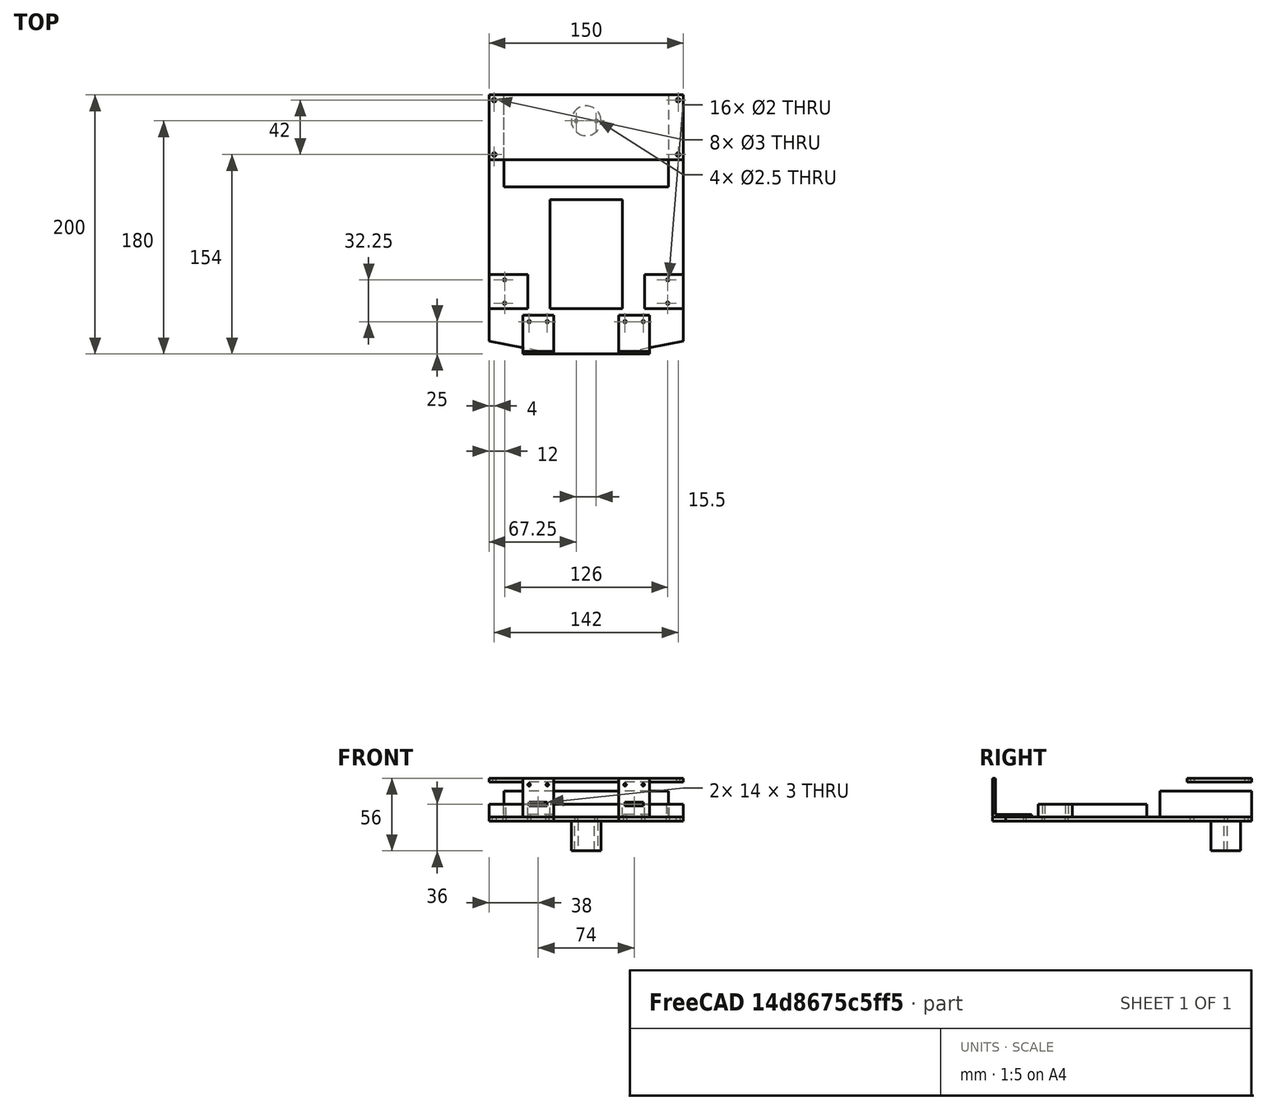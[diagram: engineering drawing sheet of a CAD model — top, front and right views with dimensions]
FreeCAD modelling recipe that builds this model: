
FCSTD DOCUMENT  (FreeCAD 0.20R29177 (Git))
Label: 3mmrobot
License: All rights reserved
LicenseURL: http://en.wikipedia.org/wiki/All_rights_reserved
objects: TechDraw::DrawViewDimension×53, PartDesign::ShapeBinder×16, PartDesign::Pad×11, PartDesign::Pocket×11, PartDesign::Body×10, TechDraw::DrawProjGroupItem×9, Sketcher::SketchObject×7, TechDraw::DrawSVGTemplate×6, TechDraw::DrawProjGroup×6, TechDraw::DrawPage×6, PartDesign::SubShapeBinder×6, TechDraw::DrawViewAnnotation×3, PartDesign::Fillet×2, App::Part×1
note: 87 computed .brp shape members not serialized (recipe doc carries the construction recipe); baked Part::Feature solids carry a one-line shape summary decoded from their .brp

FEATURE [Sketcher::SketchObject] Sketch  label="ChassisOutline"
  FullyConstrained = true
  MapMode = 5
  Support = -> [XY_Plane]
  sketch-geometry (4):
    g0: LineSegment StartX=-75 StartY=100 StartZ=0 EndX=75 EndY=100 EndZ=0
    g1: LineSegment StartX=75 StartY=100 StartZ=0 EndX=75 EndY=-100 EndZ=0
    g2: LineSegment StartX=75 StartY=-100 StartZ=0 EndX=-75 EndY=-100 EndZ=0
    g3: LineSegment StartX=-75 StartY=-100 StartZ=0 EndX=-75 EndY=100 EndZ=0
  constraints (11):
    c: Coincident(g0,g1)
    c: Coincident(g3,g0)
    c: Horizontal(g0)
    c: Vertical(g1)
    c: Vertical(g3)
    c: Distance(g0) = 150
    c: DistanceY(g2,g0) = 200
    c: Coincident(g2,g1)
    c: Coincident(g2,g3)
    c: Symmetric(g1,g0,g-1)
    c: Horizontal(g2)
FEATURE [Sketcher::SketchObject] Sketch001  label="UpperParts"
  AttachmentOffset = pos=(0,0,3) rot=(0,0,1;0rad)
  ExternalGeometry = -> [Sketch]
  FullyConstrained = true
  MapMode = 5
  Placement = pos=(0,0,3) rot=(0,0,1;0rad)
  Support = -> [XY_Plane]
  sketch-geometry (21):
    g0: LineSegment StartX=-63.5 StartY=100 StartZ=0 EndX=63.5 EndY=100 EndZ=0
    g1: LineSegment StartX=63.5 StartY=100 StartZ=0 EndX=63.5 EndY=29 EndZ=0
    g2: LineSegment StartX=63.5 StartY=29 StartZ=0 EndX=-63.5 EndY=29 EndZ=0
    g3: LineSegment StartX=-63.5 StartY=29 StartZ=0 EndX=-63.5 EndY=100 EndZ=0
    g4: LineSegment StartX=-28 StartY=19 StartZ=0 EndX=28 EndY=19 EndZ=0
    g5: LineSegment StartX=28 StartY=19 StartZ=0 EndX=28 EndY=-65 EndZ=0
    g6: LineSegment StartX=28 StartY=-65 StartZ=0 EndX=-28 EndY=-65 EndZ=0
    g7: LineSegment StartX=-28 StartY=-65 StartZ=0 EndX=-28 EndY=19 EndZ=0
    g8: LineSegment StartX=-75 StartY=-65 StartZ=0 EndX=-45 EndY=-65 EndZ=0
    g9: LineSegment StartX=-45 StartY=-65 StartZ=0 EndX=-45 EndY=-38.5 EndZ=0
    g10: LineSegment StartX=-45 StartY=-38.5 StartZ=0 EndX=-75 EndY=-38.5 EndZ=0
    g11: LineSegment StartX=-75 StartY=-38.5 StartZ=0 EndX=-75 EndY=-65 EndZ=0
    g12: LineSegment StartX=75 StartY=-38.5 StartZ=0 EndX=45 EndY=-38.5 EndZ=0
    g13: LineSegment StartX=45 StartY=-38.5 StartZ=0 EndX=45 EndY=-65 EndZ=0
    g14: LineSegment StartX=45 StartY=-65 StartZ=0 EndX=75 EndY=-65 EndZ=0
    g15: LineSegment StartX=75 StartY=-65 StartZ=0 EndX=75 EndY=-38.5 EndZ=0
    g16: Circle CenterX=-63 CenterY=-42.75 CenterZ=0 NormalX=0 NormalY=0 NormalZ=1 AngleXU=0 Radius=1
    g17: Circle CenterX=-63 CenterY=-60.75 CenterZ=0 NormalX=0 NormalY=0 NormalZ=1 AngleXU=0 Radius=1
    g18: Circle CenterX=63 CenterY=-42.75 CenterZ=0 NormalX=0 NormalY=0 NormalZ=1 AngleXU=0 Radius=1
    g19: Circle CenterX=63 CenterY=-60.75 CenterZ=0 NormalX=0 NormalY=0 NormalZ=1 AngleXU=0 Radius=1
    g20: LineSegment StartX=-45 StartY=-51.75 StartZ=0 EndX=-75 EndY=-51.75 EndZ=0
  constraints (57):
    c: Coincident(g0,g1)
    c: Coincident(g1,g2)
    c: Coincident(g2,g3)
    c: Coincident(g3,g0)
    c: Horizontal(g0)
    c: Vertical(g1)
    c: Vertical(g3)
    c: PointOnObject(g0,g-3)
    c: Coincident(g4,g5)
    c: Coincident(g5,g6)
    c: Coincident(g6,g7)
    c: Coincident(g7,g4)
    c: Horizontal(g6)
    c: Vertical(g5)
    c: Vertical(g7)
    c: Distance(g3) = 71
    c: Distance(g2) = 127
    c: Distance(g6) = 56
    c: Distance(g5) = 84
    c: DistanceY(g4,g2) = 10
    c: Symmetric(g2,g1,g-2)
    c: Symmetric(g4,g4,g-2)
    c: Coincident(g8,g9)
    c: Coincident(g9,g10)
    c: Coincident(g10,g11)
    c: Coincident(g11,g8)
    c: Horizontal(g8)
    c: Horizontal(g10)
    c: Vertical(g9)
    c: Vertical(g11)
    c: PointOnObject(g8,g-4)
    c: Coincident(g12,g13)
    c: Coincident(g13,g14)
    c: Coincident(g14,g15)
    c: Coincident(g15,g12)
    c: Horizontal(g12)
    c: Horizontal(g14)
    c: Vertical(g13)
    c: Vertical(g15)
    c: PointOnObject(g12,g-5)
    c: Horizontal(g6,g8)
    c: Equal(g13,g9)
    c: Symmetric(g9,g12,g-2)
    c: DistanceX(g10,g10) = 30
    c: DistanceY(g11,g11) = 26.5
    c: PointOnObject(g20,g9)
    c: PointOnObject(g20,g11)
    c: Symmetric(g10,g8,g20)
    c: Symmetric(g16,g17,g20)
    c: Symmetric(g16,g18,g-2)
    c: Equal(g18,g19)
    c: Equal(g19,g17)
    c: Equal(g17,g16)
    c: Diameter(g16) = 2
    c: DistanceX(g20,g16) = 12
    c: Symmetric(g19,g17,g-2)
    c: DistanceY(g17,g16) = 18
FEATURE [Sketcher::SketchObject] Sketch002  label="LowerParts"
  ExternalGeometry = -> [Sketch]
  FullyConstrained = true
  MapMode = 5
  Support = -> [XY_Plane]
  sketch-geometry (3):
    g0: Circle CenterX=0 CenterY=80 CenterZ=0 NormalX=0 NormalY=0 NormalZ=1 AngleXU=0 Radius=11.5
    g1: Circle CenterX=-7.75 CenterY=80 CenterZ=0 NormalX=0 NormalY=0 NormalZ=1 AngleXU=0 Radius=1.25
    g2: Circle CenterX=7.75 CenterY=80 CenterZ=0 NormalX=0 NormalY=0 NormalZ=1 AngleXU=0 Radius=1.25
  constraints (8):
    c: PointOnObject(g0,g-2)
    c: Symmetric(g1,g2,g-2)
    c: Horizontal(g0,g1)
    c: Diameter(g2) = 2.5
    c: Equal(g2,g1)
    c: Diameter(g0) = 23
    c: DistanceX(g1,g2) = 15.5
    c: DistanceY(g0,g-3) = 20
FEATURE [PartDesign::ShapeBinder] ShapeBinder
  Support = -> [Sketch,Sketch002,Sketch001]
  TraceSupport = false
FEATURE [PartDesign::Pad] Pad
  Direction = (0,0,1)
  Length = 3
  Length2 = 10
  Profile = -> ShapeBinder
  Type = 0
FEATURE [PartDesign::ShapeBinder] ShapeBinder001
  Support = -> [Sketch001]
  TraceSupport = false
FEATURE [PartDesign::Pocket] Pocket
  BaseFeature = -> Pad
  Direction = (0,0,-1)
  Length = 5
  Length2 = 5
  Profile = -> ShapeBinder001
  Type = 1
FEATURE [PartDesign::ShapeBinder] ShapeBinder002
  Support = -> [Sketch001]
  TraceSupport = false
FEATURE [PartDesign::Pad] Pad001
  Direction = (0,0,1)
  Length = 20
  Length2 = 10
  Profile = -> ShapeBinder002
  Type = 0
FEATURE [PartDesign::Body] Body002  label="BatteryBox"
  Group = -> [ShapeBinder002,Pad001]
  Origin = -> Origin002
  Tip = -> Pad001
FEATURE [PartDesign::ShapeBinder] ShapeBinder003
  Support = -> [Sketch001]
  TraceSupport = false
FEATURE [PartDesign::Pad] Pad002
  Direction = (0,0,1)
  Length = 10
  Length2 = 10
  Profile = -> ShapeBinder003
  Type = 0
FEATURE [PartDesign::Body] Body003  label="Breadboard"
  Group = -> [ShapeBinder003,Pad002]
  Origin = -> Origin003
  Tip = -> Pad002
FEATURE [PartDesign::ShapeBinder] ShapeBinder004
  Support = -> [Sketch001]
  TraceSupport = false
FEATURE [PartDesign::Pad] Pad003
  Direction = (0,0,1)
  Length = 10
  Length2 = 10
  Profile = -> ShapeBinder004
  Type = 0
FEATURE [PartDesign::Body] Body004  label="LeftMotor"
  Group = -> [ShapeBinder004,Pad003]
  Origin = -> Origin004
  Tip = -> Pad003
FEATURE [PartDesign::ShapeBinder] ShapeBinder005
  Support = -> [Sketch001]
  TraceSupport = false
FEATURE [PartDesign::Pad] Pad004
  Direction = (0,0,1)
  Length = 10
  Length2 = 10
  Profile = -> ShapeBinder005
  Type = 0
FEATURE [PartDesign::Body] Body005  label="RightMotor"
  Group = -> [ShapeBinder005,Pad004]
  Origin = -> Origin005
  Tip = -> Pad004
FEATURE [PartDesign::ShapeBinder] ShapeBinder006
  Support = -> [Sketch001]
  TraceSupport = false
FEATURE [PartDesign::Pocket] Pocket001
  BaseFeature = -> Pocket
  Direction = (0,0,-1)
  Length = 5
  Length2 = 5
  Profile = -> ShapeBinder006
  Type = 1
FEATURE [PartDesign::ShapeBinder] ShapeBinder007
  Support = -> [Sketch002]
  TraceSupport = false
FEATURE [PartDesign::Pocket] Pocket002
  BaseFeature = -> Pocket001
  Direction = (0,0,-1)
  Length = 5
  Length2 = 5
  Profile = -> ShapeBinder007
  Reversed = true
  Type = 1
FEATURE [PartDesign::ShapeBinder] ShapeBinder008
  Support = -> [Sketch002]
  TraceSupport = false
FEATURE [PartDesign::Pad] Pad005
  Direction = (0,0,1)
  Length = 23
  Length2 = 10
  Profile = -> ShapeBinder008
  Reversed = true
  Type = 0
FEATURE [PartDesign::Body] Body006  label="Castor"
  Group = -> [ShapeBinder008,Pad005]
  Origin = -> Origin006
  Tip = -> Pad005
FEATURE [TechDraw::DrawSVGTemplate] Template
  Height = 297
  Orientation = 0
  Width = 210
FEATURE [Sketcher::SketchObject] Sketch003  label="BevelFront"
  ExternalGeometry = -> [Sketch]
  FullyConstrained = true
  MapMode = 5
  Support = -> [XY_Plane]
  sketch-geometry (6):
    g0: LineSegment StartX=-75 StartY=-90 StartZ=0 EndX=-25 EndY=-100 EndZ=0
    g1: LineSegment StartX=25 StartY=-100 StartZ=0 EndX=75 EndY=-90 EndZ=0
    g2: LineSegment StartX=-75 StartY=-90 StartZ=0 EndX=-75 EndY=-100 EndZ=0
    g3: LineSegment StartX=-25 StartY=-100 StartZ=0 EndX=-75 EndY=-100 EndZ=0
    g4: LineSegment StartX=25 StartY=-100 StartZ=0 EndX=75 EndY=-100 EndZ=0
    g5: LineSegment StartX=75 StartY=-100 StartZ=0 EndX=75 EndY=-90 EndZ=0
  constraints (14):
    c: PointOnObject(g0,g-4)
    c: PointOnObject(g0,g-3)
    c: Symmetric(g1,g0,g-2)
    c: Symmetric(g0,g1,g-2)
    c: DistanceY(g-4,g0) = 10
    c: DistanceX(g0,g1) = 50
    c: Coincident(g2,g0)
    c: Coincident(g2,g-4)
    c: Coincident(g3,g2)
    c: Coincident(g3,g0)
    c: Coincident(g1,g4)
    c: Coincident(g4,g-5)
    c: Coincident(g4,g5)
    c: Coincident(g5,g1)
FEATURE [PartDesign::ShapeBinder] ShapeBinder009
  Support = -> [Sketch003]
  TraceSupport = false
FEATURE [PartDesign::Pocket] Pocket003
  BaseFeature = -> Pocket002
  Direction = (0,0,-1)
  Length = 5
  Length2 = 5
  Profile = -> ShapeBinder009
  Reversed = true
  Type = 1
FEATURE [PartDesign::ShapeBinder] ShapeBinder010
  Support = -> [Sketch003]
  TraceSupport = false
FEATURE [PartDesign::Pocket] Pocket004
  BaseFeature = -> Pocket003
  Direction = (0,0,-1)
  Length = 5
  Length2 = 5
  Profile = -> ShapeBinder010
  Reversed = true
  Type = 1
FEATURE [TechDraw::DrawSVGTemplate] Template001
  Height = 297
  Orientation = 0
  Width = 210
FEATURE [TechDraw::DrawProjGroupItem] ProjItem001  label="Front001"
  CoarseView = false
  Direction = (0,0,1)
  Focus = 100
  HardHidden = false
  IsoCount = 0
  IsoHidden = false
  IsoVisible = false
  LockPosition = true
  Perspective = false
  Rotation = 0
  RotationVector = (-1,0,0)
  ScaleType = 2
  SeamHidden = false
  SeamVisible = true
  SmoothHidden = false
  SmoothVisible = true
  Source = -> [Pocket002]
  Type = 0
  X = 0
  XDirection = (-1,0,0)
  Y = 0
FEATURE [TechDraw::DrawProjGroup] ProjGroup001
  Anchor = -> ProjItem001
  AutoDistribute = true
  LockPosition = false
  ProjectionType = 0
  Rotation = 0
  ScaleType = 0
  Source = -> [Pocket002]
  Views = -> [ProjItem001]
  X = 105
  Y = 148.5
  spacingX = 15
  spacingY = 15
FEATURE [TechDraw::DrawViewDimension] Dimension012
  AngleOverride = false
  Arbitrary = false
  ArbitraryTolerances = false
  EqualTolerance = true
  ExtensionAngle = 0
  FormatSpec = ⌀%.2f
  FormatSpecOverTolerance = %+.2f
  FormatSpecUnderTolerance = %+.2f
  Inverted = false
  LineAngle = 0
  LockPosition = false
  MeasureType = 1
  OverTolerance = 0
  References2D = -> [ProjItem001]
  Rotation = 0
  ScaleType = 0
  TheoreticalExact = false
  Type = 5
  UnderTolerance = 0
  X = 45.3924
  Y = 74.404
FEATURE [TechDraw::DrawViewDimension] Dimension013
  AngleOverride = false
  Arbitrary = false
  ArbitraryTolerances = false
  EqualTolerance = true
  ExtensionAngle = 0
  FormatSpec = ⌀%.2f
  FormatSpecOverTolerance = %+.2f
  FormatSpecUnderTolerance = %+.2f
  Inverted = false
  LineAngle = 0
  LockPosition = false
  MeasureType = 1
  OverTolerance = 0
  References2D = -> [ProjItem001]
  Rotation = 0
  ScaleType = 0
  TheoreticalExact = false
  Type = 5
  UnderTolerance = 0
  X = 22.3571
  Y = -61.4242
FEATURE [TechDraw::DrawPage] Page001  label="ChassisWithoutBevelsAllDimensions"
  KeepUpdated = true
  NextBalloonIndex = 1
  ProjectionType = 0
  Template = -> Template001
  Views = -> [ProjGroup001,Dimension012,Dimension013]
FEATURE [TechDraw::DrawSVGTemplate] Template002
  Height = 297
  Orientation = 0
  Width = 210
FEATURE [Sketcher::SketchObject] Sketch004  label="DaughterCardOutline"
  AttachmentOffset = pos=(0,0,30) rot=(0,0,1;0rad)
  ExternalGeometry = -> [Sketch]
  FullyConstrained = true
  MapMode = 5
  Placement = pos=(0,0,30) rot=(0,0,1;0rad)
  Support = -> [XY_Plane]
  sketch-geometry (8):
    g0: LineSegment StartX=-75 StartY=100 StartZ=0 EndX=75 EndY=100 EndZ=0
    g1: LineSegment StartX=75 StartY=100 StartZ=0 EndX=75 EndY=50 EndZ=0
    g2: LineSegment StartX=75 StartY=50 StartZ=0 EndX=-75 EndY=50 EndZ=0
    g3: LineSegment StartX=-75 StartY=50 StartZ=0 EndX=-75 EndY=100 EndZ=0
    g4: Circle CenterX=-71 CenterY=96 CenterZ=0 NormalX=0 NormalY=0 NormalZ=1 AngleXU=0 Radius=1.5
    g5: Circle CenterX=-71 CenterY=54 CenterZ=0 NormalX=0 NormalY=0 NormalZ=1 AngleXU=0 Radius=1.5
    g6: Circle CenterX=71 CenterY=96 CenterZ=0 NormalX=0 NormalY=0 NormalZ=1 AngleXU=0 Radius=1.5
    g7: Circle CenterX=71 CenterY=54 CenterZ=0 NormalX=0 NormalY=0 NormalZ=1 AngleXU=0 Radius=1.5
  constraints (22):
    c: Coincident(g0,g1)
    c: Coincident(g1,g2)
    c: Coincident(g2,g3)
    c: Coincident(g3,g0)
    c: Horizontal(g0)
    c: Horizontal(g2)
    c: Vertical(g1)
    c: Vertical(g3)
    c: Coincident(g0,g-4)
    c: PointOnObject(g1,g-5)
    c: DistanceY(g3,g3) = 50
    c: DistanceY(g4,g0) = 4
    c: DistanceX(g0,g4) = 4
    c: Vertical(g5,g4)
    c: Horizontal(g5,g7)
    c: Equal(g6,g4)
    c: Equal(g4,g5)
    c: Equal(g5,g7)
    c: Diameter(g6) = 3
    c: Vertical(g6,g7)
    c: Symmetric(g4,g6,g-2)
    c: DistanceY(g2,g5) = 4
FEATURE [PartDesign::ShapeBinder] ShapeBinder011
  Support = -> [Sketch004]
  TraceSupport = false
FEATURE [PartDesign::Pocket] Pocket005
  BaseFeature = -> Pocket004
  Direction = (0,0,-1)
  Length = 5
  Length2 = 5
  Profile = -> ShapeBinder011
  Reversed = true
  Type = 1
FEATURE [PartDesign::ShapeBinder] ShapeBinder012
  Support = -> [Sketch004]
  TraceSupport = false
FEATURE [PartDesign::Pad] Pad006
  Direction = (0,0,1)
  Length = 3
  Length2 = 10
  Profile = -> ShapeBinder012
  Type = 0
FEATURE [PartDesign::Body] Body007  label="DaughterCard"
  Group = -> [ShapeBinder012,Pad006]
  Origin = -> Origin007
  Tip = -> Pad006
FEATURE [TechDraw::DrawSVGTemplate] Template003
  Height = 297
  Orientation = 0
  Width = 210
FEATURE [TechDraw::DrawProjGroupItem] ProjItem003  label="Front003"
  CoarseView = false
  Direction = (0,0,1)
  Focus = 100
  HardHidden = false
  IsoCount = 0
  IsoHidden = false
  IsoVisible = false
  LockPosition = true
  Perspective = false
  Rotation = 0
  RotationVector = (1,0,0)
  ScaleType = 2
  SeamHidden = false
  SeamVisible = true
  SmoothHidden = false
  SmoothVisible = true
  Source = -> [Body007]
  Type = 0
  X = 0
  XDirection = (1,0,0)
  Y = 0
FEATURE [TechDraw::DrawProjGroup] ProjGroup003
  Anchor = -> ProjItem003
  AutoDistribute = true
  LockPosition = false
  ProjectionType = 0
  Rotation = 0
  ScaleType = 0
  Source = -> [Body007]
  Views = -> [ProjItem003]
  X = 104.394
  Y = 152.44
  spacingX = 15
  spacingY = 15
FEATURE [TechDraw::DrawViewDimension] Dimension028
  AngleOverride = false
  Arbitrary = false
  ArbitraryTolerances = false
  EqualTolerance = true
  ExtensionAngle = 0
  FormatSpec = %.2f
  FormatSpecOverTolerance = %+.2f
  FormatSpecUnderTolerance = %+.2f
  Inverted = false
  LineAngle = 0
  LockPosition = false
  MeasureType = 1
  OverTolerance = 0
  References2D = -> [ProjItem003]
  Rotation = 0
  ScaleType = 0
  TheoreticalExact = false
  Type = 1
  UnderTolerance = 0
  X = 0
  Y = 39.9255
FEATURE [TechDraw::DrawViewDimension] Dimension029
  AngleOverride = false
  Arbitrary = false
  ArbitraryTolerances = false
  EqualTolerance = true
  ExtensionAngle = 0
  FormatSpec = %.2f
  FormatSpecOverTolerance = %+.2f
  FormatSpecUnderTolerance = %+.2f
  Inverted = false
  LineAngle = 0
  LockPosition = false
  MeasureType = 1
  OverTolerance = 0
  References2D = -> [ProjItem003]
  Rotation = 0
  ScaleType = 0
  TheoreticalExact = false
  Type = 1
  UnderTolerance = 0
  X = -62.1643
  Y = 16.3949
FEATURE [TechDraw::DrawViewDimension] Dimension030
  AngleOverride = false
  Arbitrary = false
  ArbitraryTolerances = false
  EqualTolerance = true
  ExtensionAngle = 0
  FormatSpec = %.2f
  FormatSpecOverTolerance = %+.2f
  FormatSpecUnderTolerance = %+.2f
  Inverted = false
  LineAngle = 0
  LockPosition = false
  MeasureType = 1
  OverTolerance = 0
  References2D = -> [ProjItem003]
  Rotation = 0
  ScaleType = 0
  TheoreticalExact = false
  Type = 2
  UnderTolerance = 0
  X = -50.209
  Y = 15.356
FEATURE [TechDraw::DrawViewDimension] Dimension031
  AngleOverride = false
  Arbitrary = false
  ArbitraryTolerances = false
  EqualTolerance = true
  ExtensionAngle = 0
  FormatSpec = %.2f
  FormatSpecOverTolerance = %+.2f
  FormatSpecUnderTolerance = %+.2f
  Inverted = false
  LineAngle = 0
  LockPosition = false
  MeasureType = 1
  OverTolerance = 0
  References2D = -> [ProjItem003]
  Rotation = 0
  ScaleType = 0
  TheoreticalExact = false
  Type = 2
  UnderTolerance = 0
  X = -83.5302
  Y = 3.19164
FEATURE [TechDraw::DrawViewDimension] Dimension032
  AngleOverride = false
  Arbitrary = false
  ArbitraryTolerances = false
  EqualTolerance = true
  ExtensionAngle = 0
  FormatSpec = ⌀%.2f
  FormatSpecOverTolerance = %+.2f
  FormatSpecUnderTolerance = %+.2f
  Inverted = false
  LineAngle = 0
  LockPosition = false
  MeasureType = 1
  OverTolerance = 0
  References2D = -> [ProjItem003]
  Rotation = 0
  ScaleType = 0
  TheoreticalExact = false
  Type = 5
  UnderTolerance = 0
  X = -57.1755
  Y = -10.3746
FEATURE [TechDraw::DrawPage] Page003  label="DaughterCardDimensions"
  KeepUpdated = true
  NextBalloonIndex = 1
  ProjectionType = 0
  Template = -> Template003
  Views = -> [ProjGroup003,Dimension028,Dimension029,Dimension030,Dimension031,Dimension032]
FEATURE [App::Part] Part
  Origin = -> Origin008
FEATURE [Sketcher::SketchObject] Sketch005  label="SensorBracketBase"
  AttachmentOffset = pos=(0,0,3) rot=(0,0,1;0rad)
  ExternalGeometry = -> [Sketch]
  FullyConstrained = true
  MapMode = 5
  Placement = pos=(0,0,3) rot=(0,0,1;0rad)
  Support = -> [XY_Plane]
  sketch-geometry (13):
    g0: LineSegment StartX=-49 StartY=-100 StartZ=0 EndX=-25 EndY=-100 EndZ=0
    g1: LineSegment StartX=-25 StartY=-100 StartZ=0 EndX=-25 EndY=-70 EndZ=0
    g2: LineSegment StartX=-25 StartY=-70 StartZ=0 EndX=-49 EndY=-70 EndZ=0
    g3: LineSegment StartX=-49 StartY=-70 StartZ=0 EndX=-49 EndY=-100 EndZ=0
    g4: LineSegment StartX=25 StartY=-100 StartZ=0 EndX=49 EndY=-100 EndZ=0
    g5: LineSegment StartX=49 StartY=-100 StartZ=0 EndX=49 EndY=-70 EndZ=0
    g6: LineSegment StartX=49 StartY=-70 StartZ=0 EndX=25 EndY=-70 EndZ=0
    g7: LineSegment StartX=25 StartY=-70 StartZ=0 EndX=25 EndY=-100 EndZ=0
    g8: Circle CenterX=-30 CenterY=-75 CenterZ=0 NormalX=0 NormalY=0 NormalZ=1 AngleXU=0 Radius=1
    g9: Circle CenterX=-44 CenterY=-75 CenterZ=0 NormalX=0 NormalY=0 NormalZ=1 AngleXU=0 Radius=1
    g10: Circle CenterX=30 CenterY=-75 CenterZ=0 NormalX=0 NormalY=0 NormalZ=1 AngleXU=0 Radius=1
    g11: Circle CenterX=44 CenterY=-75 CenterZ=0 NormalX=0 NormalY=0 NormalZ=1 AngleXU=0 Radius=1
    g12: LineSegment StartX=-37 StartY=-70 StartZ=0 EndX=-37 EndY=-100 EndZ=0
  constraints (35):
    c: Coincident(g0,g1)
    c: Coincident(g1,g2)
    c: Coincident(g2,g3)
    c: Coincident(g3,g0)
    c: Horizontal(g0)
    c: Horizontal(g2)
    c: Vertical(g1)
    c: Vertical(g3)
    c: PointOnObject(g0,g-3)
    c: Coincident(g4,g5)
    c: Coincident(g5,g6)
    c: Coincident(g6,g7)
    c: Coincident(g7,g4)
    c: Horizontal(g4)
    c: Horizontal(g6)
    c: Vertical(g5)
    c: Vertical(g7)
    c: PointOnObject(g4,g-3)
    c: DistanceY(g1,g1) = 30
    c: Equal(g2,g6)
    c: Symmetric(g1,g6,g-2)
    c: DistanceX(g2,g2) = 24
    c: DistanceX(g0,g4) = 50
    c: PointOnObject(g12,g2)
    c: PointOnObject(g12,g0)
    c: Symmetric(g2,g1,g12)
    c: Symmetric(g9,g8,g12)
    c: Symmetric(g8,g10,g-2)
    c: Symmetric(g11,g9,g-2)
    c: Equal(g9,g8)
    c: Equal(g8,g10)
    c: Equal(g10,g11)
    c: Diameter(g9) = 2
    c: DistanceX(g9,g8) = 14
    c: DistanceY(g9,g2) = 5
FEATURE [PartDesign::ShapeBinder] ShapeBinder013
  Support = -> [Sketch005]
  TraceSupport = false
FEATURE [PartDesign::Pad] Pad007
  Direction = (0,0,1)
  Length = 2
  Length2 = 10
  Profile = -> ShapeBinder013
  Type = 0
FEATURE [PartDesign::ShapeBinder] ShapeBinder014
  Support = -> [Sketch005]
  TraceSupport = false
FEATURE [PartDesign::Pad] Pad008
  Direction = (0,0,1)
  Length = 2
  Length2 = 10
  Profile = -> ShapeBinder014
  Type = 0
FEATURE [Sketcher::SketchObject] Sketch007  label="SensorBracketFront"
  AttachmentOffset = pos=(0,0,100) rot=(0,0,1;0rad)
  ExternalGeometry = -> [Sketch005]
  FullyConstrained = true
  MapMode = 5
  Placement = pos=(0,-100,-2.22e-14) rot=(1,0,0;1.5708rad)
  Support = -> [XZ_Plane]
  sketch-geometry (21):
    g0: LineSegment StartX=-49 StartY=3 StartZ=0 EndX=-25 EndY=3 EndZ=0
    g1: LineSegment StartX=-25 StartY=3 StartZ=0 EndX=-25 EndY=33 EndZ=0
    g2: LineSegment StartX=-25 StartY=33 StartZ=0 EndX=-49 EndY=33 EndZ=0
    g3: LineSegment StartX=-49 StartY=33 StartZ=0 EndX=-49 EndY=3 EndZ=0
    g4: LineSegment StartX=-37 StartY=33 StartZ=0 EndX=-37 EndY=3 EndZ=0
    g5: Circle CenterX=-44 CenterY=28 CenterZ=0 NormalX=0 NormalY=0 NormalZ=1 AngleXU=0 Radius=1
    g6: Circle CenterX=-30 CenterY=28 CenterZ=0 NormalX=0 NormalY=0 NormalZ=1 AngleXU=0 Radius=1
    g7: LineSegment StartX=25 StartY=3 StartZ=0 EndX=49 EndY=3 EndZ=0
    g8: LineSegment StartX=49 StartY=3 StartZ=0 EndX=49 EndY=33 EndZ=0
    g9: LineSegment StartX=49 StartY=33 StartZ=0 EndX=25 EndY=33 EndZ=0
    g10: LineSegment StartX=25 StartY=33 StartZ=0 EndX=25 EndY=3 EndZ=0
    g11: Circle CenterX=30 CenterY=28 CenterZ=0 NormalX=0 NormalY=0 NormalZ=1 AngleXU=0 Radius=1
    g12: Circle CenterX=44 CenterY=28 CenterZ=0 NormalX=0 NormalY=0 NormalZ=1 AngleXU=0 Radius=1
    g13: LineSegment StartX=-44 StartY=11.5 StartZ=0 EndX=-30 EndY=11.5 EndZ=0
    g14: LineSegment StartX=-30 StartY=11.5 StartZ=0 EndX=-30 EndY=14.5 EndZ=0
    g15: LineSegment StartX=-30 StartY=14.5 StartZ=0 EndX=-44 EndY=14.5 EndZ=0
    g16: LineSegment StartX=-44 StartY=14.5 StartZ=0 EndX=-44 EndY=11.5 EndZ=0
    g17: LineSegment StartX=30 StartY=14.5 StartZ=0 EndX=44 EndY=14.5 EndZ=0
    g18: LineSegment StartX=44 StartY=14.5 StartZ=0 EndX=44 EndY=11.5 EndZ=0
    g19: LineSegment StartX=44 StartY=11.5 StartZ=0 EndX=30 EndY=11.5 EndZ=0
    g20: LineSegment StartX=30 StartY=11.5 StartZ=0 EndX=30 EndY=14.5 EndZ=0
  constraints (53):
    c: Coincident(g0,g1)
    c: Coincident(g1,g2)
    c: Coincident(g2,g3)
    c: Coincident(g3,g0)
    c: Horizontal(g2)
    c: Vertical(g1)
    c: Vertical(g3)
    c: Coincident(g0,g-3)
    c: Coincident(g0,g-3)
    c: DistanceY(g3,g3) = 30
    c: PointOnObject(g4,g2)
    c: PointOnObject(g4,g0)
    c: Symmetric(g1,g2,g4)
    c: Coincident(g7,g8)
    c: Coincident(g8,g9)
    c: Coincident(g9,g10)
    c: Coincident(g10,g7)
    c: Horizontal(g9)
    c: Vertical(g8)
    c: Vertical(g10)
    c: Coincident(g7,g-4)
    c: Coincident(g7,g-4)
    c: Equal(g1,g10)
    c: Symmetric(g12,g5,g-2)
    c: Symmetric(g6,g11,g-2)
    c: Equal(g5,g6)
    c: Equal(g6,g11)
    c: Equal(g11,g12)
    c: Symmetric(g6,g5,g4)
    c: Diameter(g5) = 2
    c: DistanceX(g5,g6) = 14
    c: DistanceY(g5,g2) = 5
    c: Coincident(g13,g14)
    c: Coincident(g14,g15)
    c: Coincident(g15,g16)
    c: Coincident(g16,g13)
    c: Horizontal(g15)
    c: Vertical(g14)
    c: Vertical(g16)
    c: Symmetric(g13,g13,g4)
    c: DistanceX(g13,g13) = 14
    c: DistanceY(g13,g6) = 16.5
    c: DistanceY(g14,g14) = 3
    c: Coincident(g17,g18)
    c: Coincident(g18,g19)
    c: Coincident(g19,g20)
    c: Coincident(g20,g17)
    c: Horizontal(g17)
    c: Horizontal(g19)
    c: Vertical(g18)
    c: Vertical(g20)
    c: Symmetric(g17,g14,g-2)
    c: Symmetric(g13,g18,g-2)
FEATURE [PartDesign::Body] Body  label="SketchMain"
  Group = -> [Sketch,Sketch001,Sketch002,Sketch003,Sketch004,Sketch005,Sketch007]
  Origin = -> Origin
FEATURE [PartDesign::ShapeBinder] ShapeBinder015
  Support = -> [Sketch007]
  TraceSupport = false
FEATURE [PartDesign::Pad] Pad009
  BaseFeature = -> Pad007
  Direction = (0,1,4e-16)
  Length = 2
  Length2 = 10
  Profile = -> ShapeBinder015
  Type = 0
FEATURE [PartDesign::SubShapeBinder] Binder
  BindCopyOnChange = 0
  BindMode = 0
  ClaimChildren = false
  Context = -> Body009 [Binder.]
  Fuse = false
  MakeFace = true
  OffsetFill = false
  OffsetIntersection = false
  OffsetJoinType = 0
  OffsetOpenResult = false
  PartialLoad = false
  Relative = true
  Support = -> [Body[Sketch007.Edge11,Sketch007.Edge12,Sketch007.Edge9,Sketch007.Edge10,Sketch007.Edge8,Sketch007.Edge7]]
  _Version = 2
FEATURE [PartDesign::Pad] Pad010
  BaseFeature = -> Pad008
  Direction = (0,1,4e-16)
  Length = 2
  Length2 = 10
  Profile = -> Binder
  Type = 0
FEATURE [PartDesign::SubShapeBinder] Binder001
  BindCopyOnChange = 0
  BindMode = 0
  ClaimChildren = false
  Context = -> Body008 [Binder001.]
  Fuse = false
  MakeFace = true
  OffsetFill = false
  OffsetIntersection = false
  OffsetJoinType = 0
  OffsetOpenResult = false
  PartialLoad = false
  Relative = true
  Support = -> [Body[Sketch007.Edge15,Sketch007.Edge16,Sketch007.Edge13,Sketch007.Edge14]]
  _Version = 2
FEATURE [PartDesign::Pocket] Pocket006
  BaseFeature = -> Pad009
  Direction = (0,-1,0)
  Length = 5
  Length2 = 5
  Profile = -> Binder001
  Reversed = true
  Type = 1
FEATURE [PartDesign::SubShapeBinder] Binder002
  BindCopyOnChange = 0
  BindMode = 0
  ClaimChildren = false
  Context = -> Body009 [Binder002.]
  Fuse = false
  MakeFace = true
  OffsetFill = false
  OffsetIntersection = false
  OffsetJoinType = 0
  OffsetOpenResult = false
  PartialLoad = false
  Relative = true
  Support = -> [Body[Sketch007.Edge17,Sketch007.Edge20,Sketch007.Edge19,Sketch007.Edge18]]
  _Version = 2
FEATURE [PartDesign::Pocket] Pocket007
  BaseFeature = -> Pad010
  Direction = (0,-1,0)
  Length = 5
  Length2 = 5
  Profile = -> Binder002
  Reversed = true
  Type = 1
FEATURE [PartDesign::SubShapeBinder] Binder003
  BindCopyOnChange = 0
  BindMode = 0
  ClaimChildren = false
  Context = -> Body001 [Binder003.]
  Fuse = false
  MakeFace = true
  OffsetFill = false
  OffsetIntersection = false
  OffsetJoinType = 0
  OffsetOpenResult = false
  PartialLoad = false
  Relative = true
  Support = -> [Body[Sketch005.Edge10,Sketch005.Edge9]]
  _Version = 2
FEATURE [PartDesign::Pocket] Pocket008
  BaseFeature = -> Pocket005
  Direction = (0,0,-1)
  Length = 5
  Length2 = 5
  Profile = -> Binder003
  Type = 1
FEATURE [PartDesign::SubShapeBinder] Binder004
  BindCopyOnChange = 0
  BindMode = 0
  ClaimChildren = false
  Context = -> Body001 [Binder004.]
  Fuse = false
  MakeFace = true
  OffsetFill = false
  OffsetIntersection = false
  OffsetJoinType = 0
  OffsetOpenResult = false
  PartialLoad = false
  Relative = true
  Support = -> [Body[Sketch005.Edge11,Sketch005.Edge12]]
  _Version = 2
FEATURE [PartDesign::Pocket] Pocket009
  BaseFeature = -> Pocket008
  Direction = (0,0,-1)
  Length = 5
  Length2 = 5
  Profile = -> Binder004
  Type = 1
FEATURE [PartDesign::SubShapeBinder] Binder005
  BindCopyOnChange = 0
  BindMode = 0
  ClaimChildren = false
  Context = -> Body001 [Binder005.]
  Fuse = false
  MakeFace = true
  OffsetFill = false
  OffsetIntersection = false
  OffsetJoinType = 0
  OffsetOpenResult = false
  PartialLoad = false
  Relative = true
  Support = -> [Body[Sketch004.Edge5,Sketch004.Edge6,Sketch004.Edge8,Sketch004.Vertex7,Sketch004.Edge7]]
  _Version = 2
FEATURE [PartDesign::Pocket] Pocket010
  BaseFeature = -> Pocket009
  Direction = (0,0,-1)
  Length = 5
  Length2 = 5
  Profile = -> Binder005
  Type = 1
FEATURE [PartDesign::Body] Body001  label="ChassisPlate"
  Group = -> [ShapeBinder,Pad,ShapeBinder001,Pocket,ShapeBinder006,Pocket001,ShapeBinder007,Pocket002,ShapeBinder009,Pocket003,ShapeBinder010,Pocket004,ShapeBinder011,Pocket005,Binder003,Pocket008,Binder004,Pocket009,Binder005,Pocket010]
  Origin = -> Origin001
  Tip = -> Pocket010
FEATURE [TechDraw::DrawProjGroupItem] ProjItem  label="Front"
  CoarseView = false
  Direction = (0,0,1)
  Focus = 100
  HardHidden = false
  IsoCount = 0
  IsoHidden = false
  IsoVisible = false
  LockPosition = true
  Perspective = false
  Rotation = 0
  RotationVector = (1,0,0)
  ScaleType = 2
  SeamHidden = false
  SeamVisible = true
  SmoothHidden = false
  SmoothVisible = true
  Source = -> [Body001]
  Type = 0
  X = 0
  XDirection = (-1,-1e-16,0)
  Y = 0
FEATURE [TechDraw::DrawProjGroup] ProjGroup
  Anchor = -> ProjItem
  AutoDistribute = true
  LockPosition = false
  ProjectionType = 0
  Rotation = 0
  ScaleType = 0
  Source = -> [Body001]
  Views = -> [ProjItem]
  X = 105
  Y = 148.5
  spacingX = 15
  spacingY = 15
FEATURE [TechDraw::DrawViewDimension] Dimension
  AngleOverride = false
  Arbitrary = false
  ArbitraryTolerances = false
  EqualTolerance = true
  ExtensionAngle = 0
  FormatSpec = ⌀%.2f
  FormatSpecOverTolerance = %+.2f
  FormatSpecUnderTolerance = %+.2f
  Inverted = false
  LineAngle = 0
  LockPosition = false
  MeasureType = 1
  OverTolerance = 0
  References2D = -> [ProjItem]
  Rotation = 0
  ScaleType = 0
  TheoreticalExact = false
  Type = 5
  UnderTolerance = 0
  X = 50.1529
  Y = 70.5531
FEATURE [TechDraw::DrawViewDimension] Dimension002
  AngleOverride = false
  Arbitrary = false
  ArbitraryTolerances = false
  EqualTolerance = true
  ExtensionAngle = 0
  FormatSpec = %.2f
  FormatSpecOverTolerance = %+.2f
  FormatSpecUnderTolerance = %+.2f
  Inverted = false
  LineAngle = 0
  LockPosition = false
  MeasureType = 1
  OverTolerance = 0
  References2D = -> [ProjItem]
  Rotation = 0
  ScaleType = 0
  TheoreticalExact = false
  Type = 1
  UnderTolerance = 0
  X = 2.04208
  Y = 121.051
FEATURE [TechDraw::DrawViewDimension] Dimension004
  AngleOverride = false
  Arbitrary = false
  ArbitraryTolerances = false
  EqualTolerance = true
  ExtensionAngle = 0
  FormatSpec = %.2f
  FormatSpecOverTolerance = %+.2f
  FormatSpecUnderTolerance = %+.2f
  Inverted = false
  LineAngle = 0
  LockPosition = false
  MeasureType = 1
  OverTolerance = 0
  References2D = -> [ProjItem]
  Rotation = 0
  ScaleType = 0
  TheoreticalExact = false
  Type = 1
  UnderTolerance = 0
  X = 1.29717
  Y = 110.802
FEATURE [TechDraw::DrawViewDimension] Dimension005
  AngleOverride = false
  Arbitrary = false
  ArbitraryTolerances = false
  EqualTolerance = true
  ExtensionAngle = 0
  FormatSpec = %.2f
  FormatSpecOverTolerance = %+.2f
  FormatSpecUnderTolerance = %+.2f
  Inverted = false
  LineAngle = 0
  LockPosition = false
  MeasureType = 1
  OverTolerance = 0
  References2D = -> [ProjItem]
  Rotation = 0
  ScaleType = 0
  TheoreticalExact = false
  Type = 2
  UnderTolerance = 0
  X = 83.6298
  Y = 95.1317
FEATURE [TechDraw::DrawViewDimension] Dimension006
  AngleOverride = false
  Arbitrary = false
  ArbitraryTolerances = false
  EqualTolerance = true
  ExtensionAngle = 0
  FormatSpec = %.2f
  FormatSpecOverTolerance = %+.2f
  FormatSpecUnderTolerance = %+.2f
  Inverted = false
  LineAngle = 0
  LockPosition = false
  MeasureType = 1
  OverTolerance = 0
  References2D = -> [ProjItem]
  Rotation = 0
  ScaleType = 0
  TheoreticalExact = false
  Type = 2
  UnderTolerance = 0
  X = 86.1661
  Y = 1.23328
FEATURE [TechDraw::DrawViewDimension] Dimension007
  AngleOverride = false
  Arbitrary = false
  ArbitraryTolerances = false
  EqualTolerance = true
  ExtensionAngle = 0
  FormatSpec = %.2f
  FormatSpecOverTolerance = %+.2f
  FormatSpecUnderTolerance = %+.2f
  Inverted = false
  LineAngle = 0
  LockPosition = false
  MeasureType = 1
  OverTolerance = 0
  References2D = -> [ProjItem]
  Rotation = 0
  ScaleType = 0
  TheoreticalExact = false
  Type = 2
  UnderTolerance = 0
  X = 28.9009
  Y = -87.2406
FEATURE [TechDraw::DrawViewDimension] Dimension008
  AngleOverride = false
  Arbitrary = false
  ArbitraryTolerances = false
  EqualTolerance = true
  ExtensionAngle = 0
  FormatSpec = %.2f
  FormatSpecOverTolerance = %+.2f
  FormatSpecUnderTolerance = %+.2f
  Inverted = false
  LineAngle = 0
  LockPosition = false
  MeasureType = 1
  OverTolerance = 0
  References2D = -> [ProjItem]
  Rotation = 0
  ScaleType = 0
  TheoreticalExact = false
  Type = 1
  UnderTolerance = 0
  X = 0.423435
  Y = -60.3088
FEATURE [TechDraw::DrawViewDimension] Dimension009
  AngleOverride = false
  Arbitrary = false
  ArbitraryTolerances = false
  EqualTolerance = true
  ExtensionAngle = 0
  FormatSpec = %.2f
  FormatSpecOverTolerance = %+.2f
  FormatSpecUnderTolerance = %+.2f
  Inverted = false
  LineAngle = 0
  LockPosition = false
  MeasureType = 1
  OverTolerance = 0
  References2D = -> [ProjItem]
  Rotation = 0
  ScaleType = 0
  TheoreticalExact = false
  Type = 1
  UnderTolerance = 0
  X = -69
  Y = 72.7358
FEATURE [TechDraw::DrawViewDimension] Dimension010
  AngleOverride = false
  Arbitrary = false
  ArbitraryTolerances = false
  EqualTolerance = true
  ExtensionAngle = 0
  FormatSpec = %.2f
  FormatSpecOverTolerance = %+.2f
  FormatSpecUnderTolerance = %+.2f
  Inverted = false
  LineAngle = 0
  LockPosition = false
  MeasureType = 1
  OverTolerance = 0
  References2D = -> [ProjItem]
  Rotation = 0
  ScaleType = 0
  TheoreticalExact = false
  Type = 2
  UnderTolerance = 0
  X = -52.7358
  Y = 53.9906
FEATURE [TechDraw::DrawViewDimension] Dimension011
  AngleOverride = false
  Arbitrary = false
  ArbitraryTolerances = false
  EqualTolerance = true
  ExtensionAngle = 0
  FormatSpec = %.2f
  FormatSpecOverTolerance = %+.2f
  FormatSpecUnderTolerance = %+.2f
  Inverted = false
  LineAngle = 0
  LockPosition = false
  MeasureType = 1
  OverTolerance = 0
  References2D = -> [ProjItem]
  Rotation = 0
  ScaleType = 0
  TheoreticalExact = false
  Type = 2
  UnderTolerance = 0
  X = -53.1368
  Y = 83.3939
FEATURE [TechDraw::DrawViewDimension] Dimension014
  AngleOverride = false
  Arbitrary = false
  ArbitraryTolerances = false
  EqualTolerance = true
  ExtensionAngle = 0
  FormatSpec = ⌀%.2f
  FormatSpecOverTolerance = %+.2f
  FormatSpecUnderTolerance = %+.2f
  Inverted = false
  LineAngle = 0
  LockPosition = false
  MeasureType = 1
  OverTolerance = 0
  References2D = -> [ProjItem]
  Rotation = 0
  ScaleType = 0
  TheoreticalExact = false
  Type = 5
  UnderTolerance = 0
  X = 30.6276
  Y = -55.1297
FEATURE [TechDraw::DrawViewDimension] Dimension022
  AngleOverride = false
  Arbitrary = false
  ArbitraryTolerances = false
  EqualTolerance = true
  ExtensionAngle = 0
  FormatSpec = %.2f
  FormatSpecOverTolerance = %+.2f
  FormatSpecUnderTolerance = %+.2f
  Inverted = false
  LineAngle = 0
  LockPosition = false
  MeasureType = 1
  OverTolerance = 0
  References2D = -> [ProjItem]
  Rotation = 0
  ScaleType = 0
  TheoreticalExact = false
  Type = 1
  UnderTolerance = 0
  X = -50.6554
  Y = 111.263
FEATURE [TechDraw::DrawViewDimension] Dimension023
  AngleOverride = false
  Arbitrary = false
  ArbitraryTolerances = false
  EqualTolerance = true
  ExtensionAngle = 0
  FormatSpec = %.2f
  FormatSpecOverTolerance = %+.2f
  FormatSpecUnderTolerance = %+.2f
  Inverted = false
  LineAngle = 0
  LockPosition = false
  MeasureType = 1
  OverTolerance = 0
  References2D = -> [ProjItem]
  Rotation = 0
  ScaleType = 0
  TheoreticalExact = false
  Type = 1
  UnderTolerance = 0
  X = 50
  Y = 110.28
FEATURE [TechDraw::DrawViewDimension] Dimension024
  AngleOverride = false
  Arbitrary = false
  ArbitraryTolerances = false
  EqualTolerance = true
  ExtensionAngle = 0
  FormatSpec = %.2f
  FormatSpecOverTolerance = %+.2f
  FormatSpecUnderTolerance = %+.2f
  Inverted = false
  LineAngle = 0
  LockPosition = false
  MeasureType = 1
  OverTolerance = 0
  References2D = -> [ProjItem]
  Rotation = 0
  ScaleType = 0
  TheoreticalExact = false
  Type = 1
  UnderTolerance = 0
  X = -41.0473
  Y = -60.1593
FEATURE [TechDraw::DrawPage] Page  label="CuttingDimensions"
  KeepUpdated = true
  NextBalloonIndex = 1
  ProjectionType = 0
  Template = -> Template
  Views = -> [ProjGroup,Dimension,Dimension002,Dimension004,Dimension005,Dimension006,Dimension007,Dimension008,Dimension009,Dimension010,Dimension011,Dimension014,Dimension022,Dimension023,Dimension024]
FEATURE [TechDraw::DrawProjGroupItem] ProjItem002  label="Front002"
  CoarseView = false
  Direction = (0,0,1)
  Focus = 100
  HardHidden = false
  IsoCount = 0
  IsoHidden = false
  IsoVisible = false
  LockPosition = true
  Perspective = false
  Rotation = 0
  RotationVector = (-1,0,0)
  ScaleType = 2
  SeamHidden = false
  SeamVisible = true
  SmoothHidden = false
  SmoothVisible = true
  Source = -> [Body001]
  Type = 0
  X = 0
  XDirection = (-1,0,0)
  Y = 0
FEATURE [TechDraw::DrawProjGroup] ProjGroup002
  Anchor = -> ProjItem002
  AutoDistribute = true
  LockPosition = false
  ProjectionType = 0
  Rotation = 0
  ScaleType = 0
  Source = -> [Body001]
  Views = -> [ProjItem002]
  X = 105
  Y = 148.5
  spacingX = 15
  spacingY = 15
FEATURE [TechDraw::DrawViewDimension] Dimension026
  AngleOverride = false
  Arbitrary = false
  ArbitraryTolerances = false
  EqualTolerance = true
  ExtensionAngle = 0
  FormatSpec = ⌀%.2f
  FormatSpecOverTolerance = %+.2f
  FormatSpecUnderTolerance = %+.2f
  Inverted = false
  LineAngle = 0
  LockPosition = false
  MeasureType = 1
  OverTolerance = 0
  References2D = -> [ProjItem002]
  Rotation = 0
  ScaleType = 0
  TheoreticalExact = false
  Type = 5
  UnderTolerance = 0
  X = 38.1284
  Y = 75.0527
FEATURE [TechDraw::DrawViewDimension] Dimension027
  AngleOverride = false
  Arbitrary = false
  ArbitraryTolerances = false
  EqualTolerance = true
  ExtensionAngle = 0
  FormatSpec = ⌀%.2f
  FormatSpecOverTolerance = %+.2f
  FormatSpecUnderTolerance = %+.2f
  Inverted = false
  LineAngle = 0
  LockPosition = false
  MeasureType = 1
  OverTolerance = 0
  References2D = -> [ProjItem002]
  Rotation = 0
  ScaleType = 0
  TheoreticalExact = false
  Type = 5
  UnderTolerance = 0
  X = -12.5
  Y = 69.0146
FEATURE [TechDraw::DrawSVGTemplate] Template004
  Height = 297
  Orientation = 0
  Width = 210
FEATURE [PartDesign::Fillet] Fillet
  Base = -> Pocket006 [Edge21]
  BaseFeature = -> Pocket006
  Radius = 1
  SupportTransform = false
  UseAllEdges = false
FEATURE [PartDesign::Body] Body008  label="LeftSensorBracket"
  Group = -> [ShapeBinder013,Pad007,ShapeBinder015,Pad009,Binder001,Pocket006,Fillet]
  Origin = -> Origin009
  Tip = -> Fillet
FEATURE [TechDraw::DrawProjGroupItem] ProjItem004  label="Front004"
  CoarseView = false
  Direction = (0,-1,0)
  Focus = 100
  HardHidden = false
  IsoCount = 0
  IsoHidden = false
  IsoVisible = false
  LockPosition = true
  Perspective = false
  Rotation = 0
  RotationVector = (1,0,0)
  Scale = 1.5
  ScaleType = 2
  SeamHidden = false
  SeamVisible = true
  SmoothHidden = false
  SmoothVisible = true
  Source = -> [Body008]
  Type = 0
  X = 0
  XDirection = (1,0,0)
  Y = 0
FEATURE [TechDraw::DrawProjGroupItem] ProjItem005  label="FrontTopRight"
  CoarseView = false
  Direction = (0.57735,-0.57735,0.57735)
  Focus = 100
  HardHidden = false
  IsoCount = 0
  IsoHidden = false
  IsoVisible = false
  LockPosition = false
  Perspective = false
  Rotation = 0
  RotationVector = (1,0,0)
  Scale = 1.5
  ScaleType = 2
  SeamHidden = false
  SeamVisible = true
  SmoothHidden = false
  SmoothVisible = true
  Source = -> [Body008]
  Type = 7
  X = -72.2756
  XDirection = (0.707107,0.707107,0)
  Y = -74.8153
FEATURE [TechDraw::DrawProjGroupItem] ProjItem006  label="Right"
  CoarseView = false
  Direction = (1,-1e-16,0)
  Focus = 100
  HardHidden = false
  IsoCount = 0
  IsoHidden = false
  IsoVisible = false
  LockPosition = false
  Perspective = false
  Rotation = 0
  RotationVector = (1,0,0)
  Scale = 1.5
  ScaleType = 2
  SeamHidden = false
  SeamVisible = true
  SmoothHidden = false
  SmoothVisible = true
  Source = -> [Body008]
  Type = 2
  X = -66.1378
  XDirection = (1e-16,1,0)
  Y = 0
FEATURE [PartDesign::Fillet] Fillet001
  Base = -> Pocket007 [Edge21]
  BaseFeature = -> Pocket007
  Radius = 1
  SupportTransform = false
  UseAllEdges = false
FEATURE [PartDesign::Body] Body009  label="RightSensorBracket"
  Group = -> [ShapeBinder014,Pad008,Binder,Pad010,Binder002,Pocket007,Fillet001]
  Origin = -> Origin010
  Tip = -> Fillet001
FEATURE [TechDraw::DrawViewDimension] Dimension033
  AngleOverride = false
  Arbitrary = false
  ArbitraryTolerances = false
  EqualTolerance = true
  ExtensionAngle = 0
  FormatSpec = %.2f
  FormatSpecOverTolerance = %+.2f
  FormatSpecUnderTolerance = %+.2f
  Inverted = false
  LineAngle = 0
  LockPosition = false
  MeasureType = 1
  OverTolerance = 0
  References2D = -> [ProjItem004]
  Rotation = 0
  ScaleType = 0
  TheoreticalExact = false
  Type = 1
  UnderTolerance = 0
  X = -2.05098
  Y = 34.5712
FEATURE [TechDraw::DrawViewDimension] Dimension034
  AngleOverride = false
  Arbitrary = false
  ArbitraryTolerances = false
  EqualTolerance = true
  ExtensionAngle = 0
  FormatSpec = %.2f
  FormatSpecOverTolerance = %+.2f
  FormatSpecUnderTolerance = %+.2f
  Inverted = false
  LineAngle = 0
  LockPosition = false
  MeasureType = 1
  OverTolerance = 0
  References2D = -> [ProjItem004]
  Rotation = 0
  ScaleType = 0
  TheoreticalExact = false
  Type = 1
  UnderTolerance = 0
  X = 0
  Y = 0.668294
FEATURE [TechDraw::DrawViewDimension] Dimension035
  AngleOverride = false
  Arbitrary = false
  ArbitraryTolerances = false
  EqualTolerance = true
  ExtensionAngle = 0
  FormatSpec = %.2f
  FormatSpecOverTolerance = %+.2f
  FormatSpecUnderTolerance = %+.2f
  Inverted = false
  LineAngle = 0
  LockPosition = false
  MeasureType = 1
  OverTolerance = 0
  References2D = -> [ProjItem004]
  Rotation = 0
  ScaleType = 0
  TheoreticalExact = false
  Type = 1
  UnderTolerance = 0
  X = 0.341829
  Y = 19.7781
FEATURE [TechDraw::DrawViewDimension] Dimension036
  AngleOverride = false
  Arbitrary = false
  ArbitraryTolerances = false
  EqualTolerance = true
  ExtensionAngle = 0
  FormatSpec = %.2f
  FormatSpecOverTolerance = %+.2f
  FormatSpecUnderTolerance = %+.2f
  Inverted = false
  LineAngle = 0
  LockPosition = false
  MeasureType = 1
  OverTolerance = 0
  References2D = -> [ProjItem004]
  Rotation = 0
  ScaleType = 0
  TheoreticalExact = false
  Type = 2
  UnderTolerance = 0
  X = -22.5787
  Y = 18.8572
FEATURE [TechDraw::DrawViewDimension] Dimension037
  AngleOverride = false
  Arbitrary = false
  ArbitraryTolerances = false
  EqualTolerance = true
  ExtensionAngle = 0
  FormatSpec = %.2f
  FormatSpecOverTolerance = %+.2f
  FormatSpecUnderTolerance = %+.2f
  Inverted = false
  LineAngle = 0
  LockPosition = false
  MeasureType = 1
  OverTolerance = 0
  References2D = -> [ProjItem004]
  Rotation = 0
  ScaleType = 0
  TheoreticalExact = false
  Type = 1
  UnderTolerance = 0
  X = -14.0107
  Y = 8.70284
FEATURE [TechDraw::DrawViewDimension] Dimension038
  AngleOverride = false
  Arbitrary = false
  ArbitraryTolerances = false
  EqualTolerance = true
  ExtensionAngle = 0
  FormatSpec = %.2f
  FormatSpecOverTolerance = %+.2f
  FormatSpecUnderTolerance = %+.2f
  Inverted = false
  LineAngle = 0
  LockPosition = false
  MeasureType = 1
  OverTolerance = 0
  References2D = -> [ProjItem004]
  Rotation = 0
  ScaleType = 0
  TheoreticalExact = false
  Type = 2
  UnderTolerance = 0
  X = 13.4739
  Y = -13.9774
FEATURE [TechDraw::DrawViewDimension] Dimension039
  AngleOverride = false
  Arbitrary = false
  ArbitraryTolerances = false
  EqualTolerance = true
  ExtensionAngle = 0
  FormatSpec = %.2f
  FormatSpecOverTolerance = %+.2f
  FormatSpecUnderTolerance = %+.2f
  Inverted = false
  LineAngle = 0
  LockPosition = false
  MeasureType = 1
  OverTolerance = 0
  References2D = -> [ProjItem004]
  Rotation = 0
  ScaleType = 0
  TheoreticalExact = false
  Type = 2
  UnderTolerance = 0
  X = -29.1725
  Y = 4.39281
FEATURE [TechDraw::DrawProjGroupItem] ProjItem007  label="Top"
  CoarseView = false
  Direction = (0,0,1)
  Focus = 100
  HardHidden = false
  IsoCount = 0
  IsoHidden = false
  IsoVisible = false
  LockPosition = false
  Perspective = false
  Rotation = 0
  RotationVector = (1,0,0)
  Scale = 1.5
  ScaleType = 2
  SeamHidden = false
  SeamVisible = true
  SmoothHidden = false
  SmoothVisible = true
  Source = -> [Body008]
  Type = 4
  X = 0
  XDirection = (1,0,0)
  Y = -78.4135
FEATURE [TechDraw::DrawProjGroup] ProjGroup004
  Anchor = -> ProjItem004
  AutoDistribute = true
  LockPosition = false
  ProjectionType = 0
  Rotation = 0
  Scale = 1.5
  ScaleType = 1
  Source = -> [Body008]
  Views = -> [ProjItem004,ProjItem005,ProjItem006,ProjItem007]
  X = 141.302
  Y = 167.779
  spacingX = 15
  spacingY = 15
FEATURE [TechDraw::DrawViewDimension] Dimension040
  AngleOverride = false
  Arbitrary = false
  ArbitraryTolerances = false
  EqualTolerance = true
  ExtensionAngle = 0
  FormatSpec = %.2f
  FormatSpecOverTolerance = %+.2f
  FormatSpecUnderTolerance = %+.2f
  Inverted = false
  LineAngle = 0
  LockPosition = false
  MeasureType = 1
  OverTolerance = 0
  References2D = -> [ProjItem007]
  Rotation = 0
  ScaleType = 0
  TheoreticalExact = false
  Type = 1
  UnderTolerance = 0
  X = -1.70915
  Y = 1.01572
FEATURE [TechDraw::DrawViewDimension] Dimension041
  AngleOverride = false
  Arbitrary = false
  ArbitraryTolerances = false
  EqualTolerance = true
  ExtensionAngle = 0
  FormatSpec = %.2f
  FormatSpecOverTolerance = %+.2f
  FormatSpecUnderTolerance = %+.2f
  Inverted = false
  LineAngle = 0
  LockPosition = false
  MeasureType = 1
  OverTolerance = 0
  References2D = -> [ProjItem007]
  Rotation = 0
  ScaleType = 0
  TheoreticalExact = false
  Type = 2
  UnderTolerance = 0
  X = -22.8951
  Y = 18.5281
FEATURE [TechDraw::DrawViewDimension] Dimension042
  AngleOverride = false
  Arbitrary = false
  ArbitraryTolerances = false
  EqualTolerance = true
  ExtensionAngle = 0
  FormatSpec = %.2f
  FormatSpecOverTolerance = %+.2f
  FormatSpecUnderTolerance = %+.2f
  Inverted = false
  LineAngle = 0
  LockPosition = false
  MeasureType = 1
  OverTolerance = 0
  References2D = -> [ProjItem007]
  Rotation = 0
  ScaleType = 0
  TheoreticalExact = false
  Type = 1
  UnderTolerance = 0
  X = -14.5918
  Y = 35.0277
FEATURE [TechDraw::DrawViewDimension] Dimension043
  AngleOverride = false
  Arbitrary = false
  ArbitraryTolerances = false
  EqualTolerance = true
  ExtensionAngle = 0
  FormatSpec = ⌀%.2f
  FormatSpecOverTolerance = %+.2f
  FormatSpecUnderTolerance = %+.2f
  Inverted = false
  LineAngle = 0
  LockPosition = false
  MeasureType = 1
  OverTolerance = 0
  References2D = -> [ProjItem004]
  Rotation = 0
  ScaleType = 0
  TheoreticalExact = false
  Type = 5
  UnderTolerance = 0
  X = 28.5428
  Y = 24.4408
FEATURE [TechDraw::DrawViewDimension] Dimension044
  AngleOverride = false
  Arbitrary = false
  ArbitraryTolerances = false
  EqualTolerance = true
  ExtensionAngle = 0
  FormatSpec = ⌀%.2f
  FormatSpecOverTolerance = %+.2f
  FormatSpecUnderTolerance = %+.2f
  Inverted = false
  LineAngle = 0
  LockPosition = false
  MeasureType = 1
  OverTolerance = 0
  References2D = -> [ProjItem007]
  Rotation = 0
  ScaleType = 0
  TheoreticalExact = false
  Type = 5
  UnderTolerance = 0
  X = 31.961
  Y = 34.1829
FEATURE [TechDraw::DrawViewDimension] Dimension045
  AngleOverride = false
  Arbitrary = false
  ArbitraryTolerances = false
  EqualTolerance = true
  ExtensionAngle = 0
  FormatSpec = %.2f
  FormatSpecOverTolerance = %+.2f
  FormatSpecUnderTolerance = %+.2f
  Inverted = false
  LineAngle = 0
  LockPosition = false
  MeasureType = 1
  OverTolerance = 0
  References2D = -> [ProjItem007]
  Rotation = 0
  ScaleType = 0
  TheoreticalExact = false
  Type = 2
  UnderTolerance = 0
  X = -30.8186
  Y = 3.1964
FEATURE [TechDraw::DrawViewDimension] Dimension046
  AngleOverride = false
  Arbitrary = false
  ArbitraryTolerances = false
  EqualTolerance = true
  ExtensionAngle = 0
  FormatSpec = %.2f
  FormatSpecOverTolerance = %+.2f
  FormatSpecUnderTolerance = %+.2f
  Inverted = false
  LineAngle = 0
  LockPosition = false
  MeasureType = 1
  OverTolerance = 0
  References2D = -> [ProjItem006]
  Rotation = 0
  ScaleType = 0
  TheoreticalExact = false
  Type = 1
  UnderTolerance = 0
  X = -0.545356
  Y = 32.9142
FEATURE [TechDraw::DrawViewAnnotation] Annotation  label="FrontAnnotation"
  Font = Lucida Grande
  LineSpace = 80
  LockPosition = false
  MaxWidth = -1
  Rotation = 0
  ScaleType = 0
  Text = Front
  TextSize = 5
  TextStyle = 0
  X = 142
  Y = 137.5
FEATURE [TechDraw::DrawViewAnnotation] Annotation001  label="RightAnnotation"
  Font = Lucida Grande
  LineSpace = 80
  LockPosition = false
  MaxWidth = -1
  Rotation = 0
  ScaleType = 0
  Text = Right
  TextSize = 5
  TextStyle = 0
  X = 74
  Y = 137.5
FEATURE [TechDraw::DrawViewAnnotation] Annotation002  label="TopAnnotation"
  Font = Lucida Grande
  LineSpace = 80
  LockPosition = false
  MaxWidth = -1
  Rotation = 0
  ScaleType = 0
  Text = Top
  TextSize = 5
  TextStyle = 0
  X = 141
  Y = 59.5
FEATURE [TechDraw::DrawViewDimension] Dimension047
  AngleOverride = false
  Arbitrary = false
  ArbitraryTolerances = false
  EqualTolerance = true
  ExtensionAngle = 0
  FormatSpec = %.2f
  FormatSpecOverTolerance = %+.2f
  FormatSpecUnderTolerance = %+.2f
  Inverted = false
  LineAngle = 0
  LockPosition = false
  MeasureType = 1
  OverTolerance = 0
  References2D = -> [ProjItem004]
  Rotation = 0
  ScaleType = 0
  TheoreticalExact = false
  Type = 2
  UnderTolerance = 0
  X = 21.9855
  Y = 4.625
FEATURE [TechDraw::DrawPage] Page004  label="BracketDrawings"
  KeepUpdated = true
  NextBalloonIndex = 1
  ProjectionType = 0
  Template = -> Template004
  Views = -> [ProjGroup004,Dimension033,Dimension034,Dimension035,Dimension036,Dimension037,Dimension038,Dimension039,Dimension040,Dimension041,Dimension042,Dimension043,Dimension044,Dimension045,Dimension046,Annotation,Annotation001,Annotation002,Dimension047]
FEATURE [TechDraw::DrawViewDimension] Dimension048
  AngleOverride = false
  Arbitrary = false
  ArbitraryTolerances = false
  EqualTolerance = true
  ExtensionAngle = 0
  FormatSpec = %.2f
  FormatSpecOverTolerance = %+.2f
  FormatSpecUnderTolerance = %+.2f
  Inverted = false
  LineAngle = 0
  LockPosition = false
  MeasureType = 1
  OverTolerance = 0
  References2D = -> [ProjItem002]
  Rotation = 0
  ScaleType = 0
  TheoreticalExact = false
  Type = 2
  UnderTolerance = 0
  X = -82.4306
  Y = -95.3056
FEATURE [TechDraw::DrawViewDimension] Dimension049
  AngleOverride = false
  Arbitrary = false
  ArbitraryTolerances = false
  EqualTolerance = true
  ExtensionAngle = 0
  FormatSpec = %.2f
  FormatSpecOverTolerance = %+.2f
  FormatSpecUnderTolerance = %+.2f
  Inverted = false
  LineAngle = 0
  LockPosition = false
  MeasureType = 1
  OverTolerance = 0
  References2D = -> [ProjItem002]
  Rotation = 0
  ScaleType = 0
  TheoreticalExact = false
  Type = 1
  UnderTolerance = 0
  X = -73
  Y = -106.819
FEATURE [TechDraw::DrawViewDimension] Dimension050
  AngleOverride = false
  Arbitrary = false
  ArbitraryTolerances = false
  EqualTolerance = true
  ExtensionAngle = 0
  FormatSpec = ⌀%.2f
  FormatSpecOverTolerance = %+.2f
  FormatSpecUnderTolerance = %+.2f
  Inverted = false
  LineAngle = 0
  LockPosition = false
  MeasureType = 1
  OverTolerance = 0
  References2D = -> [ProjItem002]
  Rotation = 0
  ScaleType = 0
  TheoreticalExact = false
  Type = 5
  UnderTolerance = 0
  X = -40.625
  Y = -73.2639
FEATURE [TechDraw::DrawViewDimension] Dimension051
  AngleOverride = false
  Arbitrary = false
  ArbitraryTolerances = false
  EqualTolerance = true
  ExtensionAngle = 0
  FormatSpec = %.2f
  FormatSpecOverTolerance = %+.2f
  FormatSpecUnderTolerance = %+.2f
  Inverted = false
  LineAngle = 0
  LockPosition = false
  MeasureType = 1
  OverTolerance = 0
  References2D = -> [ProjItem002]
  Rotation = 0
  ScaleType = 0
  TheoreticalExact = false
  Type = 2
  UnderTolerance = 0
  X = -17.6667
  Y = 89.1528
FEATURE [TechDraw::DrawViewDimension] Dimension052
  AngleOverride = false
  Arbitrary = false
  ArbitraryTolerances = false
  EqualTolerance = true
  ExtensionAngle = 0
  FormatSpec = %.2f
  FormatSpecOverTolerance = %+.2f
  FormatSpecUnderTolerance = %+.2f
  Inverted = false
  LineAngle = 0
  LockPosition = false
  MeasureType = 1
  OverTolerance = 0
  References2D = -> [ProjItem002]
  Rotation = 0
  ScaleType = 0
  TheoreticalExact = false
  Type = 2
  UnderTolerance = 0
  X = -67.5
  Y = -73
FEATURE [TechDraw::DrawViewDimension] Dimension053
  AngleOverride = false
  Arbitrary = false
  ArbitraryTolerances = false
  EqualTolerance = true
  ExtensionAngle = 0
  FormatSpec = %.2f
  FormatSpecOverTolerance = %+.2f
  FormatSpecUnderTolerance = %+.2f
  Inverted = false
  LineAngle = 0
  LockPosition = false
  MeasureType = 1
  OverTolerance = 0
  References2D = -> [ProjItem002]
  Rotation = 0
  ScaleType = 0
  TheoreticalExact = false
  Type = 1
  UnderTolerance = 0
  X = -59.8472
  Y = 70.2778
FEATURE [TechDraw::DrawViewDimension] Dimension054
  AngleOverride = false
  Arbitrary = false
  ArbitraryTolerances = false
  EqualTolerance = true
  ExtensionAngle = 0
  FormatSpec = %.2f
  FormatSpecOverTolerance = %+.2f
  FormatSpecUnderTolerance = %+.2f
  Inverted = false
  LineAngle = 0
  LockPosition = false
  MeasureType = 1
  OverTolerance = 0
  References2D = -> [ProjItem002]
  Rotation = 0
  ScaleType = 0
  TheoreticalExact = false
  Type = 1
  UnderTolerance = 0
  X = -37.3472
  Y = 69.9306
FEATURE [TechDraw::DrawPage] Page002  label="ChassisBevelTemplate"
  KeepUpdated = true
  NextBalloonIndex = 1
  ProjectionType = 0
  Template = -> Template002
  Views = -> [ProjGroup002,Dimension026,Dimension027,Dimension048,Dimension049,Dimension050,Dimension051,Dimension052,Dimension053,Dimension054]
FEATURE [TechDraw::DrawSVGTemplate] Template005
  Height = 297
  Orientation = 0
  Width = 210
FEATURE [TechDraw::DrawProjGroupItem] ProjItem008  label="Front005"
  CoarseView = false
  Direction = (0,0,1)
  Focus = 100
  HardHidden = false
  IsoCount = 0
  IsoHidden = false
  IsoVisible = false
  LockPosition = true
  Perspective = false
  Rotation = 0
  RotationVector = (1,0,0)
  ScaleType = 2
  SeamHidden = false
  SeamVisible = true
  SmoothHidden = false
  SmoothVisible = true
  Source = -> [Body001,Body007,Body008,Body009]
  Type = 0
  X = 0
  XDirection = (1,0,0)
  Y = 0
FEATURE [TechDraw::DrawProjGroup] ProjGroup005
  Anchor = -> ProjItem008
  AutoDistribute = true
  LockPosition = false
  ProjectionType = 0
  Rotation = 0
  ScaleType = 0
  Source = -> [Body001,Body007,Body008,Body009]
  Views = -> [ProjItem008]
  X = 105
  Y = 148.5
  spacingX = 15
  spacingY = 15
FEATURE [TechDraw::DrawViewDimension] Dimension055
  AngleOverride = false
  Arbitrary = false
  ArbitraryTolerances = false
  EqualTolerance = true
  ExtensionAngle = 0
  FormatSpec = %.2f
  FormatSpecOverTolerance = %+.2f
  FormatSpecUnderTolerance = %+.2f
  Inverted = false
  LineAngle = 0
  LockPosition = false
  MeasureType = 1
  OverTolerance = 0
  References2D = -> [ProjItem008]
  Rotation = 0
  ScaleType = 0
  TheoreticalExact = false
  Type = 2
  UnderTolerance = 0
  X = -11.8456
  Y = -84.3766
FEATURE [TechDraw::DrawViewDimension] Dimension056
  AngleOverride = false
  Arbitrary = false
  ArbitraryTolerances = false
  EqualTolerance = true
  ExtensionAngle = 0
  FormatSpec = %.2f
  FormatSpecOverTolerance = %+.2f
  FormatSpecUnderTolerance = %+.2f
  Inverted = false
  LineAngle = 0
  LockPosition = false
  MeasureType = 1
  OverTolerance = 0
  References2D = -> [ProjItem008]
  Rotation = 0
  ScaleType = 0
  TheoreticalExact = false
  Type = 1
  UnderTolerance = 0
  X = -59.2753
  Y = -64.1585
FEATURE [TechDraw::DrawViewDimension] Dimension057
  AngleOverride = false
  Arbitrary = false
  ArbitraryTolerances = false
  EqualTolerance = true
  ExtensionAngle = 0
  FormatSpec = %.2f
  FormatSpecOverTolerance = %+.2f
  FormatSpecUnderTolerance = %+.2f
  Inverted = false
  LineAngle = 0
  LockPosition = false
  MeasureType = 1
  OverTolerance = 0
  References2D = -> [ProjItem008]
  Rotation = 0
  ScaleType = 0
  TheoreticalExact = false
  Type = 1
  UnderTolerance = 0
  X = -36.7753
  Y = -64.3832
FEATURE [TechDraw::DrawViewDimension] Dimension058
  AngleOverride = false
  Arbitrary = false
  ArbitraryTolerances = false
  EqualTolerance = true
  ExtensionAngle = 0
  FormatSpec = %.2f
  FormatSpecOverTolerance = %+.2f
  FormatSpecUnderTolerance = %+.2f
  Inverted = false
  LineAngle = 0
  LockPosition = false
  MeasureType = 1
  OverTolerance = 0
  References2D = -> [ProjItem008]
  Rotation = 0
  ScaleType = 0
  TheoreticalExact = false
  Type = 1
  UnderTolerance = 0
  X = -73.4493
  Y = 68.7116
FEATURE [TechDraw::DrawViewDimension] Dimension059
  AngleOverride = false
  Arbitrary = false
  ArbitraryTolerances = false
  EqualTolerance = true
  ExtensionAngle = 0
  FormatSpec = %.2f
  FormatSpecOverTolerance = %+.2f
  FormatSpecUnderTolerance = %+.2f
  Inverted = false
  LineAngle = 0
  LockPosition = false
  MeasureType = 1
  OverTolerance = 0
  References2D = -> [ProjItem008]
  Rotation = 0
  ScaleType = 0
  TheoreticalExact = false
  Type = 2
  UnderTolerance = 0
  X = -67.5
  Y = 77
FEATURE [TechDraw::DrawViewDimension] Dimension060
  AngleOverride = false
  Arbitrary = false
  ArbitraryTolerances = false
  EqualTolerance = true
  ExtensionAngle = 0
  FormatSpec = %.2f
  FormatSpecOverTolerance = %+.2f
  FormatSpecUnderTolerance = %+.2f
  Inverted = false
  LineAngle = 0
  LockPosition = false
  MeasureType = 1
  OverTolerance = 0
  References2D = -> [ProjItem008]
  Rotation = 0
  ScaleType = 0
  TheoreticalExact = false
  Type = 2
  UnderTolerance = 0
  X = -60.4902
  Y = 87.8676
FEATURE [TechDraw::DrawViewDimension] Dimension061
  AngleOverride = false
  Arbitrary = false
  ArbitraryTolerances = false
  EqualTolerance = true
  ExtensionAngle = 0
  FormatSpec = ⌀%.2f
  FormatSpecOverTolerance = %+.2f
  FormatSpecUnderTolerance = %+.2f
  Inverted = false
  LineAngle = 0
  LockPosition = false
  MeasureType = 1
  OverTolerance = 0
  References2D = -> [ProjItem008]
  Rotation = 0
  ScaleType = 0
  TheoreticalExact = false
  Type = 5
  UnderTolerance = 0
  X = 51.4502
  Y = 90.094
FEATURE [TechDraw::DrawViewDimension] Dimension062
  AngleOverride = false
  Arbitrary = false
  ArbitraryTolerances = false
  EqualTolerance = true
  ExtensionAngle = 0
  FormatSpec = ⌀%.2f
  FormatSpecOverTolerance = %+.2f
  FormatSpecUnderTolerance = %+.2f
  Inverted = false
  LineAngle = 0
  LockPosition = false
  MeasureType = 1
  OverTolerance = 0
  References2D = -> [ProjItem008]
  Rotation = 0
  ScaleType = 0
  TheoreticalExact = false
  Type = 5
  UnderTolerance = 0
  X = -13.9297
  Y = -64.9306
FEATURE [TechDraw::DrawPage] Page005
  KeepUpdated = true
  NextBalloonIndex = 1
  ProjectionType = 0
  Template = -> Template005
  Views = -> [ProjGroup005,Dimension055,Dimension056,Dimension057,Dimension058,Dimension059,Dimension060,Dimension061,Dimension062]
